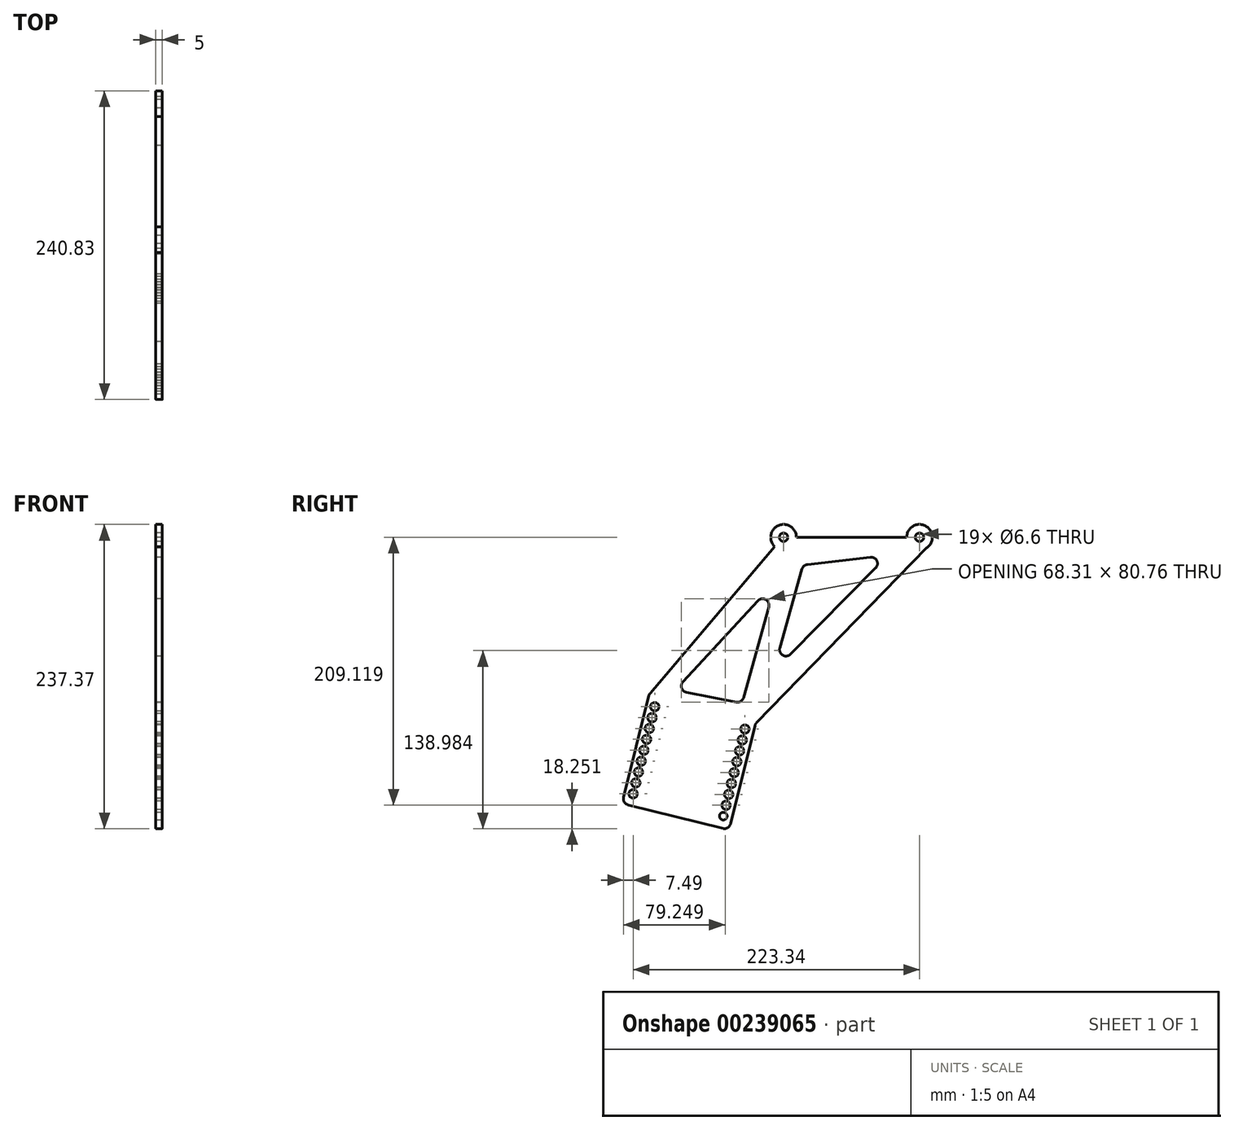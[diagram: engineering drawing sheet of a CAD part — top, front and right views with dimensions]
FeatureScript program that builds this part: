
annotation { "Feature Type Name" : "Feature", "Feature Type Description" : "" }
export const myFeature = defineFeature(function(context is Context, id is Id, definition is map)
    precondition{}
    {
        {
            var Q0;
            Q0=qCreatedBy(makeId("Right.planeOp"),FACE);
            var sketch = newSketch(context, id + "F0", { "sketchPlane" : qUnion([Q0])});
            skArc(sketch, "E0", {"start": v(109.3, 0) * mm, "mid": v(106, 3.3) * mm, "end": v(102.7, 0) * mm});
            skCircle(sketch, "E1", {"center": v(0, 0) * mm, "radius": 3.3 * mm});
            skPoint(sketch, "E2.orphan", {"position": v(0, -3.3) * mm});
            skArc(sketch, "E3", {"start": v(102.7, 0) * mm, "mid": v(106, -3.3) * mm, "end": v(109.3, 0) * mm});
            skArc(sketch, "E4", {"start": v(10, 0) * mm, "mid": v(-3.92, 9.2) * mm, "end": v(-6.92, -7.22) * mm});
            skArc(sketch, "E5", {"start": v(111.38, -8.43) * mm, "mid": v(110.8, 8.77) * mm, "end": v(96, 0) * mm});
            skLineSegment(sketch, "E6", {"start": v(10, 0) * mm, "end": v(96, 0) * mm});
            skPoint(sketch, "E7.trimOffspring.end.orphan", {"position": v(0, 3.45) * mm});
            skLineSegment(sketch, "E8", {"start": v(111.38, -8.43) * mm, "end": v(-21.06, -144.65) * mm});
            skLineSegment(sketch, "E9", {"start": v(-6.92, -7.22) * mm, "end": v(-103.96, -121.53) * mm});
            skCircle(sketch, "E10", {"center": v(-46.97, -217.61) * mm, "radius": 3 * mm});
            skLineSegment(sketch, "E11", {"start": v(0, 0) * mm, "end": v(-0.7, -3.23) * mm});
            skLineSegment(sketch, "E12", {"start": v(-24.97, -157.62) * mm, "end": v(-41.33, -223.57) * mm});
            skPoint(sketch, "E13.start.orphan", {"position": v(-43.97, -217.61) * mm});
            skCircle(sketch, "E14", {"center": v(-30.12, -149.67) * mm, "radius": 3.3 * mm});
            skCircle(sketch, "E15", {"center": v(-100.49, -132.22) * mm, "radius": 3.3 * mm});
            skCircle(sketch, "E16", {"center": v(-117.34, -200.16) * mm, "radius": 3.3 * mm});
            skLineSegment(sketch, "E17", {"start": v(-105, -123.56) * mm, "end": v(-124.68, -202.9) * mm});
            skLineSegment(sketch, "E18", {"start": v(-121.03, -208.95) * mm, "end": v(-47.39, -227.22) * mm});
            skPoint(sketch, "E19.visualSharp", {"position": v(-125.89, -207.75) * mm});
            skArc(sketch, "E19.filletArc", {"start": v(-124.68, -202.9) * mm, "mid": v(-124.11, -206.68) * mm, "end": v(-121.03, -208.95) * mm});
            skPoint(sketch, "E20.visualSharp", {"position": v(-42.54, -228.42) * mm});
            skArc(sketch, "E20.filletArc", {"start": v(-47.39, -227.22) * mm, "mid": v(-43.6, -226.65) * mm, "end": v(-41.33, -223.57) * mm});
            skCircle(sketch, "E21", {"center": v(-108.91, -166.19) * mm, "radius": 3.3 * mm});
            skCircle(sketch, "E22", {"center": v(-38.55, -183.64) * mm, "radius": 3.3 * mm});
            skPoint(sketch, "E23.visualSharp", {"position": v(-104.72, -122.43) * mm});
            skArc(sketch, "E23.filletArc", {"start": v(-103.96, -121.53) * mm, "mid": v(-104.6, -122.49) * mm, "end": v(-105, -123.56) * mm});
            skCircle(sketch, "E24", {"center": v(-104.7, -149.2) * mm, "radius": 3.3 * mm});
            skCircle(sketch, "E25", {"center": v(-42.76, -200.63) * mm, "radius": 3.3 * mm});
            skCircle(sketch, "E26", {"center": v(-113.13, -183.17) * mm, "radius": 3.3 * mm});
            skCircle(sketch, "E27", {"center": v(-34.34, -166.66) * mm, "radius": 3.3 * mm});
            skCircle(sketch, "E28", {"center": v(-102.6, -140.7) * mm, "radius": 3.3 * mm});
            skCircle(sketch, "E29", {"center": v(-106.8, -157.7) * mm, "radius": 3.3 * mm});
            skCircle(sketch, "E30", {"center": v(-111.02, -174.68) * mm, "radius": 3.3 * mm});
            skCircle(sketch, "E31", {"center": v(-115.23, -191.67) * mm, "radius": 3.3 * mm});
            skCircle(sketch, "E32", {"center": v(-32.23, -158.16) * mm, "radius": 3.3 * mm});
            skCircle(sketch, "E33", {"center": v(-36.44, -175.15) * mm, "radius": 3.3 * mm});
            skCircle(sketch, "E34", {"center": v(-40.66, -192.13) * mm, "radius": 3.3 * mm});
            skCircle(sketch, "E35", {"center": v(-44.87, -209.12) * mm, "radius": 3.3 * mm});
            skLineSegment(sketch, "E36", {"start": v(-24.97, -157.62) * mm, "end": v(-22.32, -146.93) * mm});
            skPoint(sketch, "E37.visualSharp", {"position": v(-22, -145.62) * mm});
            skArc(sketch, "E37.filletArc", {"start": v(-21.06, -144.65) * mm, "mid": v(-21.84, -145.7) * mm, "end": v(-22.32, -146.93) * mm});
            skLineSegment(sketch, "E38", {"start": v(-31.18, -125.1) * mm, "end": v(-11.6, -54.28) * mm});
            skLineSegment(sketch, "E39", {"start": v(-20.1, -49.55) * mm, "end": v(-78.42, -112.74) * mm});
            skLineSegment(sketch, "E40", {"start": v(-75.7, -121.04) * mm, "end": v(-36.97, -128.67) * mm});
            skLineSegment(sketch, "E41", {"start": v(-2.93, -86.4) * mm, "end": v(14.33, -24.88) * mm});
            skLineSegment(sketch, "E42", {"start": v(18.56, -21.27) * mm, "end": v(67.65, -15.55) * mm});
            skLineSegment(sketch, "E43", {"start": v(71.78, -24.03) * mm, "end": v(5.45, -91.26) * mm});
            skPoint(sketch, "E44.visualSharp", {"position": v(-84.48, -119.3) * mm});
            skArc(sketch, "E44.filletArc", {"start": v(-78.42, -112.74) * mm, "mid": v(-79.5, -117.68) * mm, "end": v(-75.7, -121.04) * mm});
            skPoint(sketch, "E45.visualSharp", {"position": v(-32.42, -129.57) * mm});
            skArc(sketch, "E45.filletArc", {"start": v(-36.97, -128.67) * mm, "mid": v(-33.38, -128.02) * mm, "end": v(-31.18, -125.1) * mm});
            skPoint(sketch, "E46.visualSharp", {"position": v(-6.1, -34.4) * mm});
            skArc(sketch, "E46.filletArc", {"start": v(-11.6, -54.28) * mm, "mid": v(-13.99, -48.57) * mm, "end": v(-20.1, -49.55) * mm});
            skPoint(sketch, "E47.visualSharp", {"position": v(15.23, -21.65) * mm});
            skArc(sketch, "E47.filletArc", {"start": v(18.56, -21.27) * mm, "mid": v(15.9, -22.43) * mm, "end": v(14.33, -24.88) * mm});
            skPoint(sketch, "E48.visualSharp", {"position": v(-8.16, -105.04) * mm});
            skArc(sketch, "E48.filletArc", {"start": v(-2.93, -86.4) * mm, "mid": v(-0.62, -92.07) * mm, "end": v(5.45, -91.26) * mm});
            skPoint(sketch, "E49.visualSharp", {"position": v(81.77, -13.9) * mm});
            skArc(sketch, "E49.filletArc", {"start": v(71.78, -24.03) * mm, "mid": v(72.72, -18.33) * mm, "end": v(67.65, -15.55) * mm});
            skSolve(sketch);
        }
        {
            var Q0;
            Q0 = qSketchRegion(id + "F0", true);
            extrude(context, id + "F1", {"entities" : qUnion([Q0]), "depth" : 5 * mm});
        }
    });
